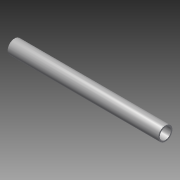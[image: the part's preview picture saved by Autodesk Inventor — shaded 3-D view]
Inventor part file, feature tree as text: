
AUTODESK INVENTOR PART (.ipt)
format: ipt  version: 2014 (Build 180170000, 170)  size: 100,864 bytes
history: native  units: in
note: dims shown in document units (in); Inventor stores cm internally (conversion verified against a paired STEP export)
features: other x2, extrude x1, imported_body x1, sketch x1
ambient origin geometry x8: Origin, YZ Plane, XZ Plane, XY Plane, X Axis, Y Axis, Z Axis, Center Point
bodies: Body1 (feature_tree)
feature tree (5):
  parser-record x1  (decoder bookkeeping rows leaked as tree rows — omitted from the tree; the rows remain in map.json)
  other  "4347K3111"
  extrude  "Extrusion2"  [1 undecoded]
  imported_body  "Base1"
  sketch  "Sketch2"  dims[d2=3.0in d3=0.0in]
note: 1 required parameter value undecoded (feature->parameter linkage not recoverable at this tier; creation-order binding heuristic only, values carry confidence <= 0.55)
